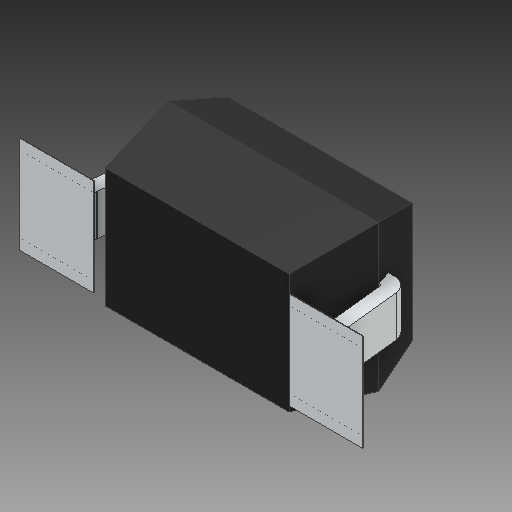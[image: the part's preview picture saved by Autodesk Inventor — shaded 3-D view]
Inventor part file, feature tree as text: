
AUTODESK INVENTOR PART (.ipt)
format: ipt  version: 2018 (Build 220112000, 112)  size: 167,936 bytes
history: native  units: mm
features: fillet x1
ambient origin geometry x8: Origin, YZ Plane, XZ Plane, XY Plane, X Axis, Y Axis, Z Axis, Center Point
bodies: Volumenkörper1 (feature_tree)
feature tree (1):
  fillet  "Fillet2"  [1 undecoded]
note: 1 required parameter value undecoded (feature->parameter linkage not recoverable at this tier; creation-order binding heuristic only, values carry confidence <= 0.55)
